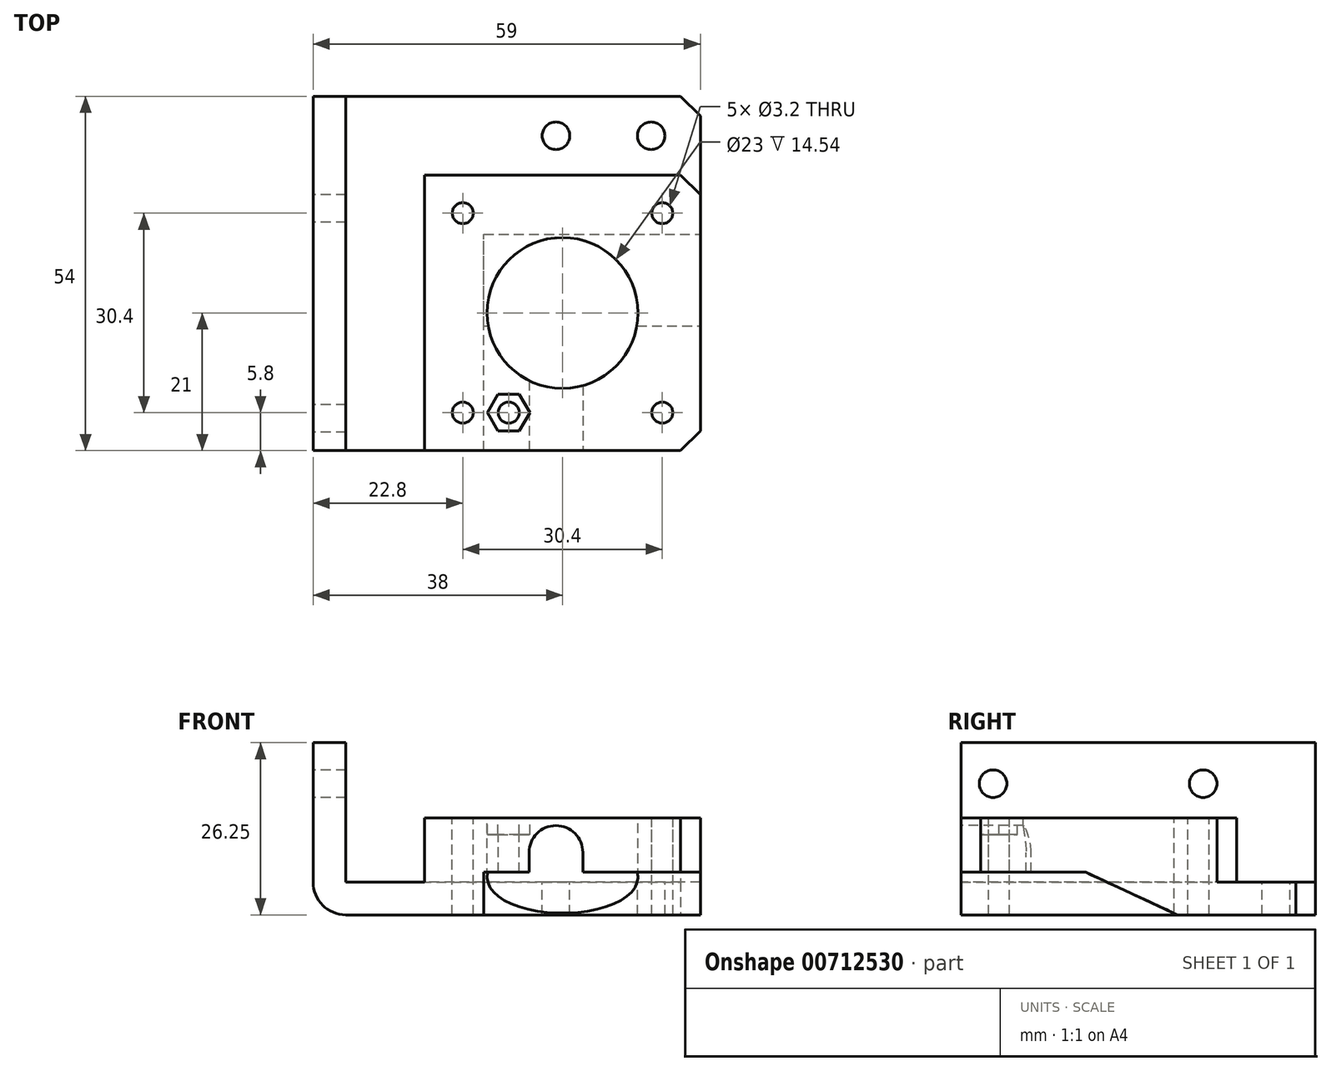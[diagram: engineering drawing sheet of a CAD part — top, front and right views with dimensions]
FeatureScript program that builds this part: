
annotation { "Feature Type Name" : "Feature", "Feature Type Description" : "" }
export const myFeature = defineFeature(function(context is Context, id is Id, definition is map)
    precondition{}
    {
        {
            var Q0;
            Q0=qCreatedBy(makeId("Top.planeOp"),FACE);
            var sketch = newSketch(context, id + "F0", { "sketchPlane" : qUnion([Q0])});
            skLineSegment(sketch, "E0.bottom", {"start": v(0, 0) * mm, "end": v(59, 0) * mm});
            skLineSegment(sketch, "E0.top", {"start": v(0, 54) * mm, "end": v(59, 54) * mm});
            skLineSegment(sketch, "E0.left", {"start": v(0, 0) * mm, "end": v(0, 54) * mm});
            skLineSegment(sketch, "E0.right", {"start": v(59, 0) * mm, "end": v(59, 54) * mm});
            skSolve(sketch);
        }
        {
            var Q0;
            Q0=makeQuery(id+"F0.imprint","IMPRINT",FACE,{"disambiguationData":[TD([[makeQuery(id+"F0.imprint","IMPRINT",EDGE,{"derivedFrom":sQuery(id+"F0.wireOp",EDGE,"E0.bottom")}),1.0]])]});
            extrude(context, id + "F1", {"entities" : qUnion([Q0]), "depth" : 5 * mm, "offsetDistance" : 25 * mm});
        }
        {
            var Q0;
            Q0=makeQuery(id+"F1.opExtrude","CAP_FACE",FACE,{"disambiguationData":[OSD([sQuery(id+"F0.wireOp",EDGE,"E0.bottom"),sQuery(id+"F0.wireOp",EDGE,"E0.top"),sQuery(id+"F0.wireOp",EDGE,"E0.left"),sQuery(id+"F0.wireOp",EDGE,"E0.right")])],"isStart":false});
            var sketch = newSketch(context, id + "F2", { "sketchPlane" : qUnion([Q0])});
            skLineSegment(sketch, "E1.bottom", {"start": v(0, 54) * mm, "end": v(5, 54) * mm});
            skLineSegment(sketch, "E1.top", {"start": v(0, 0) * mm, "end": v(5, 0) * mm});
            skLineSegment(sketch, "E1.left", {"start": v(0, 54) * mm, "end": v(0, 0) * mm});
            skLineSegment(sketch, "E1.right", {"start": v(5, 54) * mm, "end": v(5, 0) * mm});
            skSolve(sketch);
        }
        {
            var Q0;
            Q0=makeQuery(id+"F2.imprint","IMPRINT",FACE,{"disambiguationData":[TD([[makeQuery(id+"F2.imprint","IMPRINT",EDGE,{"derivedFrom":sQuery(id+"F2.wireOp",EDGE,"E1.bottom")}),-1.0]])]});
            extrude(context, id + "F3", {"entities" : qUnion([Q0]), "operationType" : NewBodyOperationType.ADD, "depth" : 21.25 * mm, "offsetDistance" : 25 * mm});
        }
        {
            var Q0;
            Q0=makeQuery(id+"F1.opExtrude","CAP_FACE",FACE,{"disambiguationData":[OSD([sQuery(id+"F0.wireOp",EDGE,"E0.bottom"),sQuery(id+"F0.wireOp",EDGE,"E0.top"),sQuery(id+"F0.wireOp",EDGE,"E0.left"),sQuery(id+"F0.wireOp",EDGE,"E0.right")])],"isStart":false});
            var sketch = newSketch(context, id + "F4", { "sketchPlane" : qUnion([Q0])});
            skLineSegment(sketch, "E2.bottom", {"start": v(59, 0) * mm, "end": v(17, 0) * mm});
            skLineSegment(sketch, "E2.top", {"start": v(59, 42) * mm, "end": v(17, 42) * mm});
            skLineSegment(sketch, "E2.left", {"start": v(59, 0) * mm, "end": v(59, 42) * mm});
            skLineSegment(sketch, "E2.right", {"start": v(17, 0) * mm, "end": v(17, 42) * mm});
            skSolve(sketch);
        }
        {
            var Q0;
            Q0=makeQuery(id+"F4.imprint","IMPRINT",FACE,{"disambiguationData":[TD([[makeQuery(id+"F4.imprint","IMPRINT",EDGE,{"derivedFrom":sQuery(id+"F4.wireOp",EDGE,"E2.bottom")}),1.0]])]});
            extrude(context, id + "F5", {"entities" : qUnion([Q0]), "operationType" : NewBodyOperationType.ADD, "depth" : 9.75 * mm, "offsetDistance" : 25 * mm});
        }
        {
            var Q0;
            Q0=makeQuery(id+"F5.boolean.opBoolean","MERGE",FACE,{"derivedFrom":[makeQuery(id+"F1.opExtrude","SWEPT_FACE",FACE,{"disambiguationData":[OSD([sQuery(id+"F0.wireOp",EDGE,"E0.right")])]}),makeQuery(id+"F5.opExtrude","SWEPT_FACE",FACE,{"disambiguationData":[OSD([sQuery(id+"F4.wireOp",EDGE,"E2.left")])]})]});
            var sketch = newSketch(context, id + "F6", { "sketchPlane" : qUnion([Q0])});
            skLineSegment(sketch, "E3", {"start": v(0, 0) * mm, "end": v(0, 6.5) * mm});
            skLineSegment(sketch, "E4", {"start": v(0, 6.5) * mm, "end": v(19, 6.5) * mm});
            skLineSegment(sketch, "E5", {"start": v(19, 6.5) * mm, "end": v(33, 0) * mm});
            skLineSegment(sketch, "E6", {"start": v(33, 0) * mm, "end": v(0, 0) * mm});
            skSolve(sketch);
        }
        {
            var Q0;
            Q0=makeQuery(id+"F6.imprint","IMPRINT",FACE,{"disambiguationData":[TD([[makeQuery(id+"F6.imprint","IMPRINT",EDGE,{"derivedFrom":sQuery(id+"F6.wireOp",EDGE,"E3")}),1.0]])]});
            extrude(context, id + "F7", {"entities" : qUnion([Q0]), "operationType" : NewBodyOperationType.REMOVE, "oppositeDirection" : true, "depth" : 33 * mm, "offsetDistance" : 25 * mm});
        }
        {
            var Q0;
            Q0=makeQuery(id+"F5.opExtrude","CAP_FACE",FACE,{"disambiguationData":[OSD([sQuery(id+"F4.wireOp",EDGE,"E2.bottom"),sQuery(id+"F4.wireOp",EDGE,"E2.top"),sQuery(id+"F4.wireOp",EDGE,"E2.left"),sQuery(id+"F4.wireOp",EDGE,"E2.right")])],"isStart":false});
            var sketch = newSketch(context, id + "F8", { "sketchPlane" : qUnion([Q0])});
            skCircle(sketch, "E7", {"center": v(38, 21) * mm, "radius": 11.5 * mm});
            skCircle(sketch, "E8", {"center": v(22.8, 36.2) * mm, "radius": 1.6 * mm});
            skCircle(sketch, "E9", {"center": v(53.2, 36.2) * mm, "radius": 1.6 * mm});
            skCircle(sketch, "E10", {"center": v(22.8, 5.8) * mm, "radius": 1.6 * mm});
            skCircle(sketch, "E11", {"center": v(53.2, 5.8) * mm, "radius": 1.6 * mm});
            skCircle(sketch, "E12", {"center": v(29.8, 5.8) * mm, "radius": 1.6 * mm});
            skSolve(sketch);
        }
        {
            var Q0;
            Q0=makeQuery(id+"F8.imprint","IMPRINT",FACE,{"disambiguationData":[TD([[makeQuery(id+"F8.imprint","IMPRINT",EDGE,{"derivedFrom":sQuery(id+"F8.wireOp",EDGE,"E8")}),1.0]])]});
            var Q1;
            Q1=makeQuery(id+"F8.imprint","IMPRINT",FACE,{"disambiguationData":[TD([[makeQuery(id+"F8.imprint","IMPRINT",EDGE,{"derivedFrom":sQuery(id+"F8.wireOp",EDGE,"E7")}),1.0]])]});
            var Q2;
            Q2=makeQuery(id+"F8.imprint","IMPRINT",FACE,{"disambiguationData":[TD([[makeQuery(id+"F8.imprint","IMPRINT",EDGE,{"derivedFrom":sQuery(id+"F8.wireOp",EDGE,"E9")}),1.0]])]});
            var Q3;
            Q3=makeQuery(id+"F8.imprint","IMPRINT",FACE,{"disambiguationData":[TD([[makeQuery(id+"F8.imprint","IMPRINT",EDGE,{"derivedFrom":sQuery(id+"F8.wireOp",EDGE,"E10")}),1.0]])]});
            var Q4;
            Q4=makeQuery(id+"F8.imprint","IMPRINT",FACE,{"disambiguationData":[TD([[makeQuery(id+"F8.imprint","IMPRINT",EDGE,{"derivedFrom":sQuery(id+"F8.wireOp",EDGE,"E11")}),1.0]])]});
            var Q5;
            Q5=makeQuery(id+"F8.imprint","IMPRINT",FACE,{"disambiguationData":[TD([[makeQuery(id+"F8.imprint","IMPRINT",EDGE,{"derivedFrom":sQuery(id+"F8.wireOp",EDGE,"E12")}),1.0]])]});
            extrude(context, id + "F9", {"entities" : qUnion([Q0, Q1, Q2, Q3, Q4, Q5]), "operationType" : NewBodyOperationType.REMOVE, "endBound" : BoundingType.THROUGH_ALL, "oppositeDirection" : true, "depth" : 25 * mm, "offsetDistance" : 25 * mm});
        }
        {
            var Q0;
            Q0=makeQuery(id+"F1.opExtrude","CAP_FACE",FACE,{"disambiguationData":[OSD([sQuery(id+"F0.wireOp",EDGE,"E0.bottom"),sQuery(id+"F0.wireOp",EDGE,"E0.top"),sQuery(id+"F0.wireOp",EDGE,"E0.left"),sQuery(id+"F0.wireOp",EDGE,"E0.right")])],"isStart":false});
            var sketch = newSketch(context, id + "F10", { "sketchPlane" : qUnion([Q0])});
            skCircle(sketch, "E13", {"center": v(37, 48) * mm, "radius": 2.1 * mm});
            skCircle(sketch, "E14", {"center": v(51.5, 48) * mm, "radius": 2.1 * mm});
            skSolve(sketch);
        }
        {
            var Q0;
            Q0=makeQuery(id+"F10.imprint","IMPRINT",FACE,{"disambiguationData":[TD([[makeQuery(id+"F10.imprint","IMPRINT",EDGE,{"derivedFrom":sQuery(id+"F10.wireOp",EDGE,"E13")}),1.0]])]});
            var Q1;
            Q1=makeQuery(id+"F10.imprint","IMPRINT",FACE,{"disambiguationData":[TD([[makeQuery(id+"F10.imprint","IMPRINT",EDGE,{"derivedFrom":sQuery(id+"F10.wireOp",EDGE,"E14")}),1.0]])]});
            extrude(context, id + "F11", {"entities" : qUnion([Q0, Q1]), "operationType" : NewBodyOperationType.REMOVE, "endBound" : BoundingType.THROUGH_ALL, "oppositeDirection" : true, "depth" : 25 * mm, "offsetDistance" : 25 * mm});
        }
        {
            var Q0;
            Q0=makeQuery(id+"F1.opExtrude","SWEPT_EDGE",EDGE,{"disambiguationData":[OSD([sQuery(id+"F0.wireOp",EDGE,"E0.top"),sQuery(id+"F0.wireOp",EDGE,"E0.right")])]});
            var Q1;
            Q1=makeQuery(id+"F5.opExtrude","SWEPT_EDGE",EDGE,{"disambiguationData":[OSD([sQuery(id+"F0.wireOp",EDGE,"E0.right"),sQuery(id+"F4.wireOp",EDGE,"E2.top"),sQuery(id+"F4.wireOp",EDGE,"E2.left")])]});
            var Q2;
            Q2=makeQuery(id+"F5.boolean.opBoolean","MERGE",EDGE,{"derivedFrom":[makeQuery(id+"F1.opExtrude","SWEPT_EDGE",EDGE,{"disambiguationData":[OSD([sQuery(id+"F0.wireOp",EDGE,"E0.bottom"),sQuery(id+"F0.wireOp",EDGE,"E0.right")])]}),makeQuery(id+"F5.opExtrude","SWEPT_EDGE",EDGE,{"disambiguationData":[OSD([sQuery(id+"F4.wireOp",EDGE,"E2.bottom"),sQuery(id+"F4.wireOp",EDGE,"E2.left")])]})]});
            chamfer(context, id + "F12", {"entities" : qUnion([Q0, Q1, Q2]), "width" : 3 * mm, "tangentPropagation" : true});
        }
        {
            var Q0;
            Q0=makeQuery(id+"F1.opExtrude","CAP_EDGE",EDGE,{"disambiguationData":[OSD([sQuery(id+"F0.wireOp",EDGE,"E0.left")])],"isStart":true});
            fillet(context, id + "F13", {"entities" : qUnion([Q0]), "radius" : 5 * mm, "tangentPropagation" : true, "allowEdgeOverflow" : false});
        }
        {
            var Q0;
            Q0=makeQuery(id+"F5.opExtrude","CAP_FACE",FACE,{"disambiguationData":[OSD([sQuery(id+"F4.wireOp",EDGE,"E2.bottom"),sQuery(id+"F4.wireOp",EDGE,"E2.top"),sQuery(id+"F4.wireOp",EDGE,"E2.left"),sQuery(id+"F4.wireOp",EDGE,"E2.right")])],"isStart":false});
            var sketch = newSketch(context, id + "F14", { "sketchPlane" : qUnion([Q0])});
            skCircle(sketch, "E15.cCircle", {"center": v(29.8, 5.8) * mm, "radius": 2.8 * mm, "construction": true});
            skLineSegment(sketch, "E15.0", {"start": v(33.03, 5.8) * mm, "end": v(31.42, 3) * mm});
            skLineSegment(sketch, "E15.1", {"start": v(31.42, 3) * mm, "end": v(28.18, 3) * mm});
            skLineSegment(sketch, "E15.2", {"start": v(28.18, 3) * mm, "end": v(26.57, 5.8) * mm});
            skLineSegment(sketch, "E15.3", {"start": v(26.57, 5.8) * mm, "end": v(28.18, 8.6) * mm});
            skLineSegment(sketch, "E15.4", {"start": v(28.18, 8.6) * mm, "end": v(31.42, 8.6) * mm});
            skLineSegment(sketch, "E15.5", {"start": v(31.42, 8.6) * mm, "end": v(33.03, 5.8) * mm});
            skPoint(sketch, "E15.0.midPoint", {"position": v(32.23, 4.4) * mm});
            skSolve(sketch);
        }
        {
            var Q0;
            Q0=makeQuery(id+"F14.imprint","IMPRINT",FACE,{"disambiguationData":[TD([[makeQuery(id+"F14.imprint","IMPRINT",EDGE,{"derivedFrom":sQuery(id+"F14.wireOp",EDGE,"E15.0")}),-1.0]])]});
            extrude(context, id + "F15", {"entities" : qUnion([Q0]), "operationType" : NewBodyOperationType.REMOVE, "oppositeDirection" : true, "depth" : 2.5 * mm, "offsetDistance" : 25 * mm});
        }
        {
            var Q0;
            Q0=makeQuery(id+"F3.boolean.opBoolean","MERGE",FACE,{"derivedFrom":[makeQuery(id+"F1.opExtrude","SWEPT_FACE",FACE,{"disambiguationData":[OSD([sQuery(id+"F0.wireOp",EDGE,"E0.left")])]}),makeQuery(id+"F3.opExtrude","SWEPT_FACE",FACE,{"disambiguationData":[OSD([sQuery(id+"F2.wireOp",EDGE,"E1.left")])]})]});
            var sketch = newSketch(context, id + "F16", { "sketchPlane" : qUnion([Q0])});
            skCircle(sketch, "E16", {"center": v(-36.9, 20) * mm, "radius": 2.1 * mm});
            skCircle(sketch, "E17", {"center": v(-4.9, 20) * mm, "radius": 2.1 * mm});
            skSolve(sketch);
        }
        {
            var Q0;
            Q0=makeQuery(id+"F16.imprint","IMPRINT",FACE,{"disambiguationData":[TD([[makeQuery(id+"F16.imprint","IMPRINT",EDGE,{"derivedFrom":sQuery(id+"F16.wireOp",EDGE,"E16")}),1.0]])]});
            var Q1;
            Q1=makeQuery(id+"F16.imprint","IMPRINT",FACE,{"disambiguationData":[TD([[makeQuery(id+"F16.imprint","IMPRINT",EDGE,{"derivedFrom":sQuery(id+"F16.wireOp",EDGE,"E17")}),1.0]])]});
            extrude(context, id + "F17", {"entities" : qUnion([Q0, Q1]), "operationType" : NewBodyOperationType.REMOVE, "endBound" : BoundingType.THROUGH_ALL, "oppositeDirection" : true, "depth" : 25 * mm, "offsetDistance" : 25 * mm});
        }
        {
            var Q0;
            Q0=makeQuery(id+"F5.boolean.opBoolean","MERGE",FACE,{"derivedFrom":[makeQuery(id+"F3.boolean.opBoolean","MERGE",FACE,{"derivedFrom":[makeQuery(id+"F1.opExtrude","SWEPT_FACE",FACE,{"disambiguationData":[OSD([sQuery(id+"F0.wireOp",EDGE,"E0.bottom")])]}),makeQuery(id+"F3.opExtrude","SWEPT_FACE",FACE,{"disambiguationData":[OSD([sQuery(id+"F2.wireOp",EDGE,"E1.top")])]})]}),makeQuery(id+"F5.opExtrude","SWEPT_FACE",FACE,{"disambiguationData":[OSD([sQuery(id+"F4.wireOp",EDGE,"E2.bottom")])]})]});
            var sketch = newSketch(context, id + "F18", { "sketchPlane" : qUnion([Q0])});
            skLineSegment(sketch, "E18.top", {"start": v(32.9, 6.5) * mm, "end": v(41.1, 6.5) * mm});
            skLineSegment(sketch, "E18.left", {"start": v(32.9, 9.5) * mm, "end": v(32.9, 6.5) * mm});
            skLineSegment(sketch, "E18.right", {"start": v(41.1, 9.5) * mm, "end": v(41.1, 6.5) * mm});
            skArc(sketch, "E19.trimOffspring", {"start": v(41.1, 9.5) * mm, "mid": v(37, 13.6) * mm, "end": v(32.9, 9.5) * mm});
            skSolve(sketch);
        }
        {
            var Q0;
            Q0=makeQuery(id+"F18.imprint","IMPRINT",FACE,{"disambiguationData":[TD([[makeQuery(id+"F18.imprint","IMPRINT",EDGE,{"derivedFrom":sQuery(id+"F18.wireOp",EDGE,"E18.top")}),1.0]])]});
            extrude(context, id + "F19", {"entities" : qUnion([Q0]), "operationType" : NewBodyOperationType.REMOVE, "endBound" : BoundingType.UP_TO_NEXT, "oppositeDirection" : true, "depth" : 25 * mm, "offsetDistance" : 25 * mm});
        }
    });
